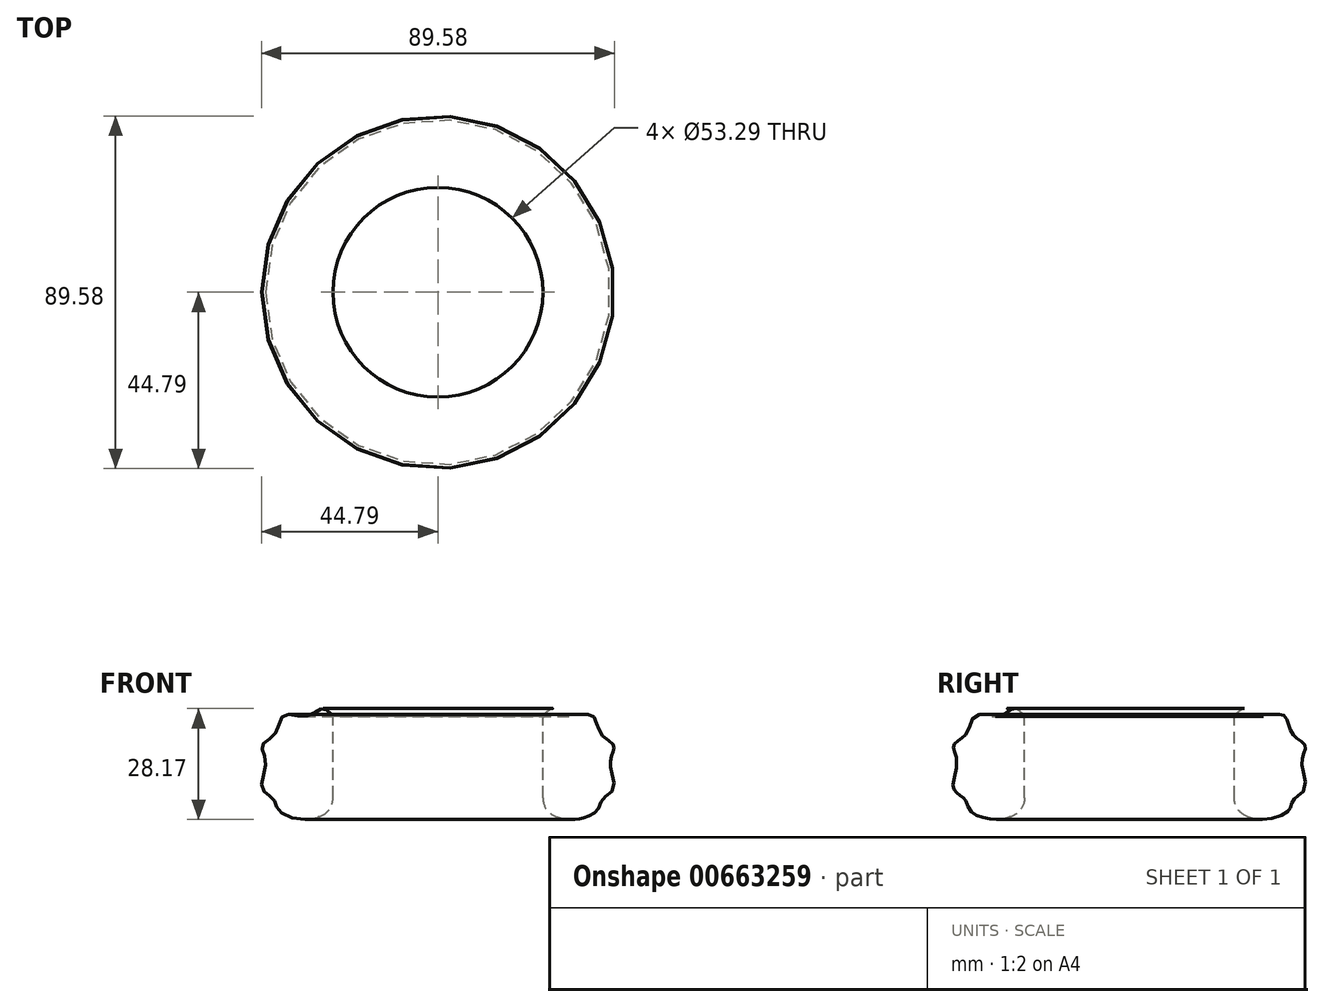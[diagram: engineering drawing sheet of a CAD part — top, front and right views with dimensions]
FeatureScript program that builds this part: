
annotation { "Feature Type Name" : "Feature", "Feature Type Description" : "" }
export const myFeature = defineFeature(function(context is Context, id is Id, definition is map)
    precondition{}
    {
        {
            var Q0;
            Q0=qCreatedBy(makeId("Front.planeOp"),FACE);
            var sketch = newSketch(context, id + "F0", { "sketchPlane" : qUnion([Q0])});
            skArc(sketch, "E0", {"start": v(-21.22, 22.42) * mm, "mid": v(-11.37, 16.35) * mm, "end": v(0, 14.23) * mm});
            skArc(sketch, "E1", {"start": v(-21.22, 22.42) * mm, "mid": v(-23.77, 24.22) * mm, "end": v(-26.67, 25.35) * mm});
            skLineSegment(sketch, "E2", {"start": v(0, 0) * mm, "end": v(0, 14.23) * mm});
            skLineSegment(sketch, "E3", {"start": v(0, 0) * mm, "end": v(-29.87, 0) * mm});
            skLineSegment(sketch, "E4", {"start": v(-29.87, 0) * mm, "end": v(-29.87, 0) * mm});
            skFitSpline(sketch, "E5", {"points": [v(-26.67, 25.35) * mm, v(-29.3, 27.2) * mm, v(-33.24, 25.3) * mm, v(-39.2, 25.45) * mm, v(-41.41, 20.83) * mm, v(-44.65, 17.87) * mm, v(-43.82, 13.71) * mm, v(-44.65, 6.87) * mm, v(-41.78, 4.2) * mm, v(-40.21, 1.05) * mm, v(-29.87, 0) * mm, v(-28.38, 17.6) * mm], "startDerivative": vector(-37.98, 42.98) * mm, "endDerivative": vector(-20.92, 144.15) * mm});
            skSolve(sketch);
        }
        {
            var Q0;
            Q0 = qSketchRegion(id + "F0", true);
            var Q1;
            Q1=sQuery(id+"F0.wireOp",EDGE,"E2");
            revolve(context, id + "F1", {"entities" : qUnion([Q0]), "axis" : qUnion([Q1]), "revolveType" : RevolveType.FULL});
        }
        {
            var Q0;
            Q0=qCreatedBy(makeId("Top.planeOp"),FACE);
            cPlane(context, id + "F2", {"entities" : qUnion([Q0]), "cplaneType" : CPlaneType.OFFSET, "offset" : 30 * mm, "width" : 150 * mm, "height" : 150 * mm});
        }
        {
            var Q0;
            Q0=qCreatedBy(id+"F2.planeOp",FACE);
            var sketch = newSketch(context, id + "F3", { "sketchPlane" : qUnion([Q0])});
            skCircle(sketch, "E6", {"center": v(0, 0) * mm, "radius": 26.64 * mm});
            skSolve(sketch);
        }
        {
            var Q0;
            Q0=makeQuery(id+"F3.imprint","IMPRINT",FACE,{"disambiguationData":[TD([[makeQuery(id+"F3.imprint","IMPRINT",EDGE,{"derivedFrom":sQuery(id+"F3.wireOp",EDGE,"E6")}),1.0]])]});
            var Q1;
            Q1=sQuery(id+"F3.wireOp",EDGE,"E6");
            extrude(context, id + "F4", {"entities" : qUnion([Q0]), "operationType" : NewBodyOperationType.REMOVE, "surfaceEntities" : qUnion([Q1]), "endBound" : BoundingType.THROUGH_ALL, "oppositeDirection" : true, "depth" : 33 * mm, "offsetDistance" : 25 * mm});
        }
        {
            var Q0;
            Q0=makeQuery(id+"F1.opRevolve","SWEPT_EDGE",EDGE,{"disambiguationData":[OSD([sQuery(id+"F0.wireOp",EDGE,"E3"),sQuery(id+"F0.wireOp",EDGE,"E5")])]});
            fillet(context, id + "F5", {"entities" : qUnion([Q0]), "radius" : 5 * mm, "tangentPropagation" : true, "allowEdgeOverflow" : false});
        }
        {
            var Q0;
            Q0=makeQuery(id+"F4.boolean.opBoolean","INTERSECT",EDGE,{"derivedFrom":[makeQuery(id+"F1.opRevolve","SWEPT_FACE",FACE,{"disambiguationData":[OSD([sQuery(id+"F0.wireOp",EDGE,"E3")])]}),makeQuery(id+"F4.opExtrude","SWEPT_FACE",FACE,{"disambiguationData":[OSD([sQuery(id+"F3.wireOp",EDGE,"E6")])]})]});
            fillet(context, id + "F6", {"entities" : qUnion([Q0]), "radius" : 5 * mm, "tangentPropagation" : true, "allowEdgeOverflow" : false});
        }
        {
            var Q0;
            Q0=makeQuery(id+"F4.boolean.opBoolean","INTERSECT",EDGE,{"derivedFrom":[makeQuery(id+"F1.opRevolve","SWEPT_FACE",FACE,{"disambiguationData":[OSD([sQuery(id+"F0.wireOp",EDGE,"E1")])]}),makeQuery(id+"F4.opExtrude","SWEPT_FACE",FACE,{"disambiguationData":[OSD([sQuery(id+"F3.wireOp",EDGE,"E6")])]})]});
            fillet(context, id + "F7", {"entities" : qUnion([Q0]), "radius" : 5 * mm, "tangentPropagation" : true, "allowEdgeOverflow" : false});
        }
    });
